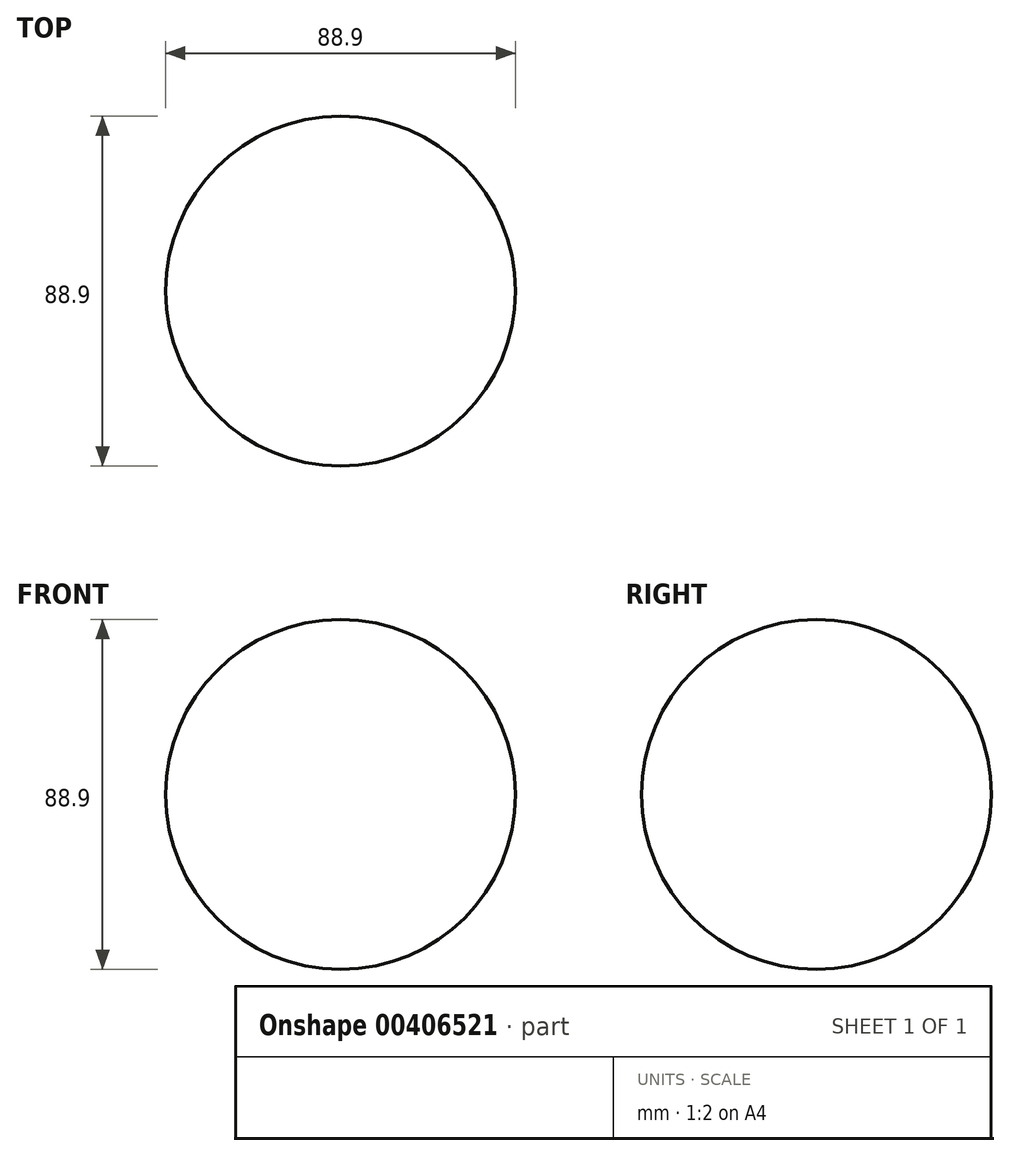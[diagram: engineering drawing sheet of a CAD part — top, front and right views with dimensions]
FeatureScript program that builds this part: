
annotation { "Feature Type Name" : "Feature", "Feature Type Description" : "" }
export const myFeature = defineFeature(function(context is Context, id is Id, definition is map)
    precondition{}
    {
        {
            var Q0;
            Q0=qCreatedBy(makeId("Top.planeOp"),FACE);
            var sketch = newSketch(context, id + "F0", { "sketchPlane" : qUnion([Q0])});
            skLineSegment(sketch, "E0.bottom", {"start": v(-112.33, 26.42) * mm, "end": v(-23.43, 26.42) * mm});
            skLineSegment(sketch, "E0.top", {"start": v(-112.33, -62.48) * mm, "end": v(-23.43, -62.48) * mm});
            skLineSegment(sketch, "E0.left", {"start": v(-112.33, 26.42) * mm, "end": v(-112.33, -62.48) * mm});
            skLineSegment(sketch, "E0.right", {"start": v(-23.43, 26.42) * mm, "end": v(-23.43, -62.48) * mm});
            skSolve(sketch);
        }
        {
            var Q0;
            Q0=makeQuery(id+"F0.imprint","IMPRINT",FACE,{"disambiguationData":[TD([[makeQuery(id+"F0.imprint","IMPRINT",EDGE,{"derivedFrom":sQuery(id+"F0.wireOp",EDGE,"E0.bottom")}),-1.0]])]});
            extrude(context, id + "F1", {"entities" : qUnion([Q0]), "depth" : 88.9 * mm});
        }
        {
            var Q0;
            Q0=makeQuery(id+"F1.opExtrude","SWEPT_EDGE",EDGE,{"disambiguationData":[OSD([sQuery(id+"F0.wireOp",EDGE,"E0.top"),sQuery(id+"F0.wireOp",EDGE,"E0.left")])]});
            var Q1;
            Q1=makeQuery(id+"F1.opExtrude","SWEPT_EDGE",EDGE,{"disambiguationData":[OSD([sQuery(id+"F0.wireOp",EDGE,"E0.bottom"),sQuery(id+"F0.wireOp",EDGE,"E0.left")])]});
            var Q2;
            Q2=makeQuery(id+"F1.opExtrude","CAP_EDGE",EDGE,{"disambiguationData":[OSD([sQuery(id+"F0.wireOp",EDGE,"E0.left")])],"isStart":false});
            var Q3;
            Q3=makeQuery(id+"F1.opExtrude","CAP_EDGE",EDGE,{"disambiguationData":[OSD([sQuery(id+"F0.wireOp",EDGE,"E0.left")])],"isStart":true});
            var Q4;
            Q4=makeQuery(id+"F1.opExtrude","CAP_EDGE",EDGE,{"disambiguationData":[OSD([sQuery(id+"F0.wireOp",EDGE,"E0.top")])],"isStart":false});
            var Q5;
            Q5=makeQuery(id+"F1.opExtrude","CAP_EDGE",EDGE,{"disambiguationData":[OSD([sQuery(id+"F0.wireOp",EDGE,"E0.bottom")])],"isStart":false});
            var Q6;
            Q6=makeQuery(id+"F1.opExtrude","CAP_EDGE",EDGE,{"disambiguationData":[OSD([sQuery(id+"F0.wireOp",EDGE,"E0.right")])],"isStart":false});
            var Q7;
            Q7=makeQuery(id+"F1.opExtrude","CAP_EDGE",EDGE,{"disambiguationData":[OSD([sQuery(id+"F0.wireOp",EDGE,"E0.right")])],"isStart":true});
            var Q8;
            Q8=makeQuery(id+"F1.opExtrude","SWEPT_EDGE",EDGE,{"disambiguationData":[OSD([sQuery(id+"F0.wireOp",EDGE,"E0.bottom"),sQuery(id+"F0.wireOp",EDGE,"E0.right")])]});
            var Q9;
            Q9=makeQuery(id+"F1.opExtrude","SWEPT_EDGE",EDGE,{"disambiguationData":[OSD([sQuery(id+"F0.wireOp",EDGE,"E0.top"),sQuery(id+"F0.wireOp",EDGE,"E0.right")])]});
            var Q10;
            Q10=makeQuery(id+"F1.opExtrude","CAP_EDGE",EDGE,{"disambiguationData":[OSD([sQuery(id+"F0.wireOp",EDGE,"E0.top")])],"isStart":true});
            var Q11;
            Q11=makeQuery(id+"F1.opExtrude","CAP_EDGE",EDGE,{"disambiguationData":[OSD([sQuery(id+"F0.wireOp",EDGE,"E0.bottom")])],"isStart":true});
            fillet(context, id + "F2", {"entities" : qUnion([Q0, Q1, Q2, Q3, Q4, Q5, Q6, Q7, Q8, Q9, Q10, Q11]), "radius" : 44.45 * mm, "tangentPropagation" : true, "allowEdgeOverflow" : false});
        }
    });
